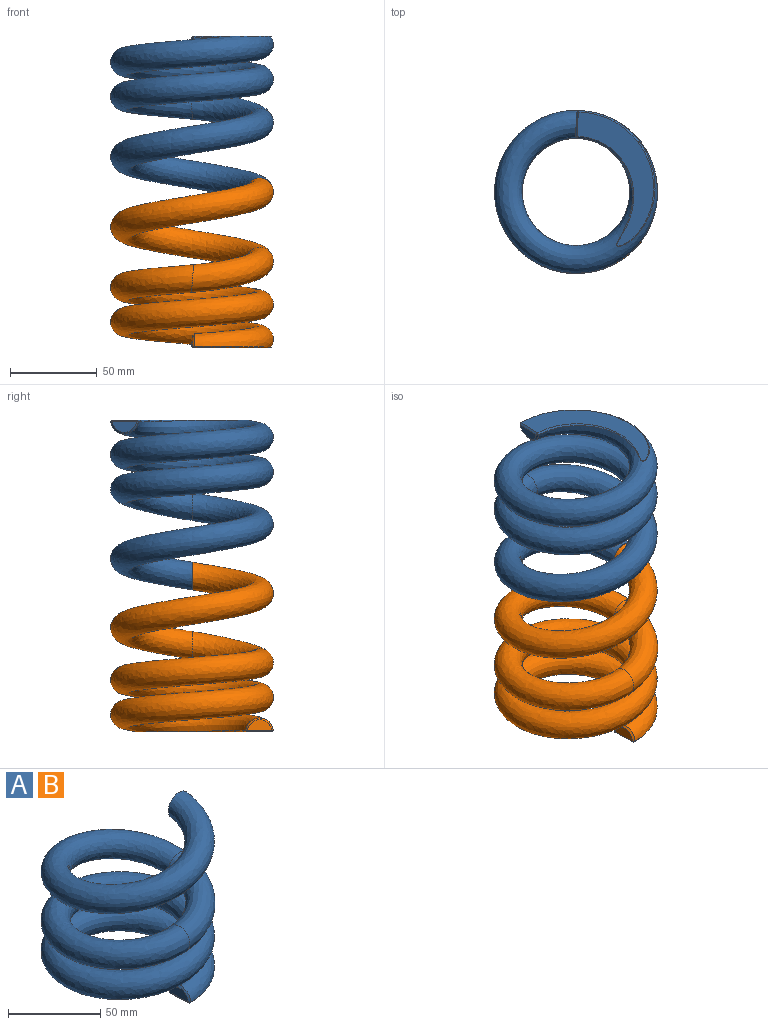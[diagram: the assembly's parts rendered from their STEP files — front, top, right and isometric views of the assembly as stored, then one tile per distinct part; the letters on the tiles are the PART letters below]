
ASSEMBLY  parts=2 mates=1
PART A: 17 faces, bbox 112.2x112.2x108.1 mm
  f0: plane 18.23x18.23mm, normal (0,1,0), area 201.1mm2, adj f1
  f1: bspline ~110x110mm, area 12397mm2, adj f0,f2
  f2: bspline ~47.63x46.89mm, area 3115.9mm2, adj f1,f4
  f3: plane 14.02x6.35mm, normal (-1,-0.05,0.07), area 64.2mm2, adj f6,f7,f9,f14
  f4: bspline ~93.75x93.75mm, area 22865.1mm2, adj f2,f6,f8,f12,f16
  f5: plane 77.58x44.76mm, normal (0,0,-1), area 1072.7mm2, adj f7,f8,f10,f13
  f6: bspline ~16.06x9.43mm, area 29.8mm2, adj f3,f4,f9,f12,f14,f16
  f7: plane 14.13x1.54mm, normal (-0.73,-0.03,-0.68), area 18.6mm2, adj f3,f5,f9,f10,f13,f14
  f8: bspline ~78.41x46.16mm, area 176.9mm2, adj f4,f5,f10,f12,f13,f16
  f9: bspline ~1.41x1.34mm, area 0.5mm2, adj f3,f6,f7,f11
  f10: bspline ~1.11x1.07mm, area 0.4mm2, adj f5,f7,f8,f11
  f11: sphere r=0.5mm, area 0.1mm2, adj f9,f10,f12
  f12: bspline ~1.39x1.36mm, area 0.5mm2, adj f4,f6,f8,f11
  f13: bspline ~1.09x1.08mm, area 0.4mm2, adj f5,f7,f8,f15
  f14: bspline ~1.22x1.21mm, area 0.5mm2, adj f3,f6,f7,f15
  f15: sphere r=0.5mm, area 0.1mm2, adj f13,f14,f16
  f16: bspline ~1.23x1.2mm, area 0.5mm2, adj f4,f6,f8,f15
PART B: same geometry as A
PLACE A rot(axis=(1,0,0),180deg) t=(0,0,0)mm
PLACE B t=(0,0,-80)mm
MATE fastened A.f0 <-> B.f0  axis (0,-1,0) through (39,0,-40)mm
